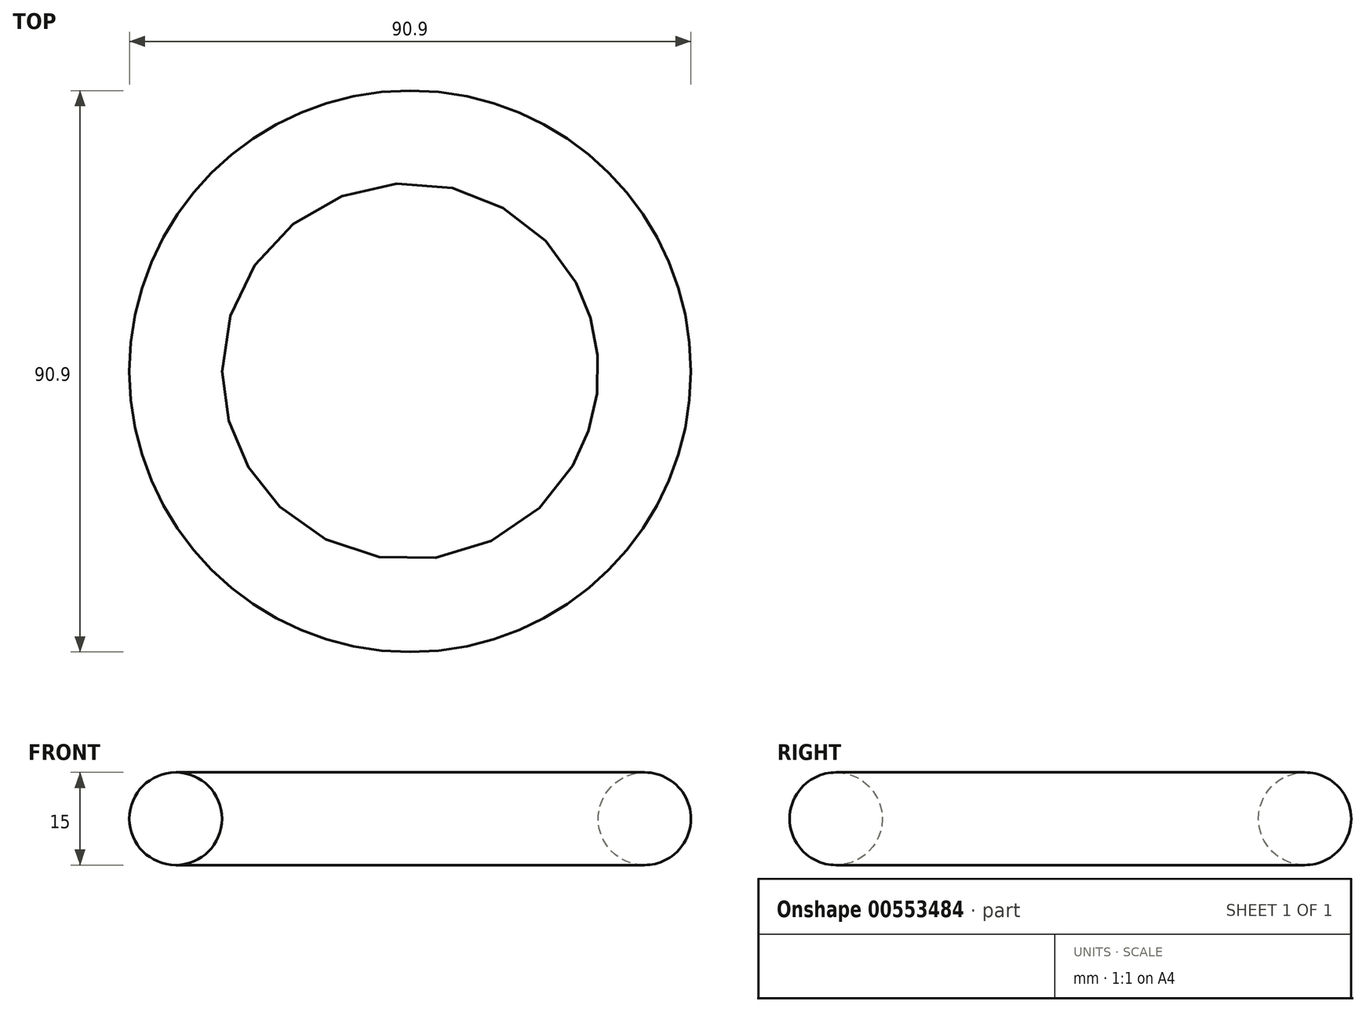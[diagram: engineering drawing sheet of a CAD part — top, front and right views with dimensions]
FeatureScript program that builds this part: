
annotation { "Feature Type Name" : "Feature", "Feature Type Description" : "" }
export const myFeature = defineFeature(function(context is Context, id is Id, definition is map)
    precondition{}
    {
        {
            var Q0;
            Q0=qCreatedBy(makeId("Front.planeOp"),FACE);
            var sketch = newSketch(context, id + "F0", { "sketchPlane" : qUnion([Q0])});
            skCircle(sketch, "E0", {"center": v(37.95, 0) * mm, "radius": 7.5 * mm});
            skLineSegment(sketch, "E1", {"start": v(0, 0) * mm, "end": v(0, 34.6) * mm, "construction": true});
            skSolve(sketch);
        }
        {
            var Q0;
            Q0=makeQuery(id+"F0.imprint","IMPRINT",FACE,{"disambiguationData":[TD([[makeQuery(id+"F0.imprint","IMPRINT",EDGE,{"derivedFrom":sQuery(id+"F0.wireOp",EDGE,"E0")}),1.0]])]});
            var Q1;
            Q1=sQuery(id+"F0.wireOp",EDGE,"E1");
            revolve(context, id + "F1", {"entities" : qUnion([Q0]), "axis" : qUnion([Q1]), "revolveType" : RevolveType.FULL});
        }
    });
